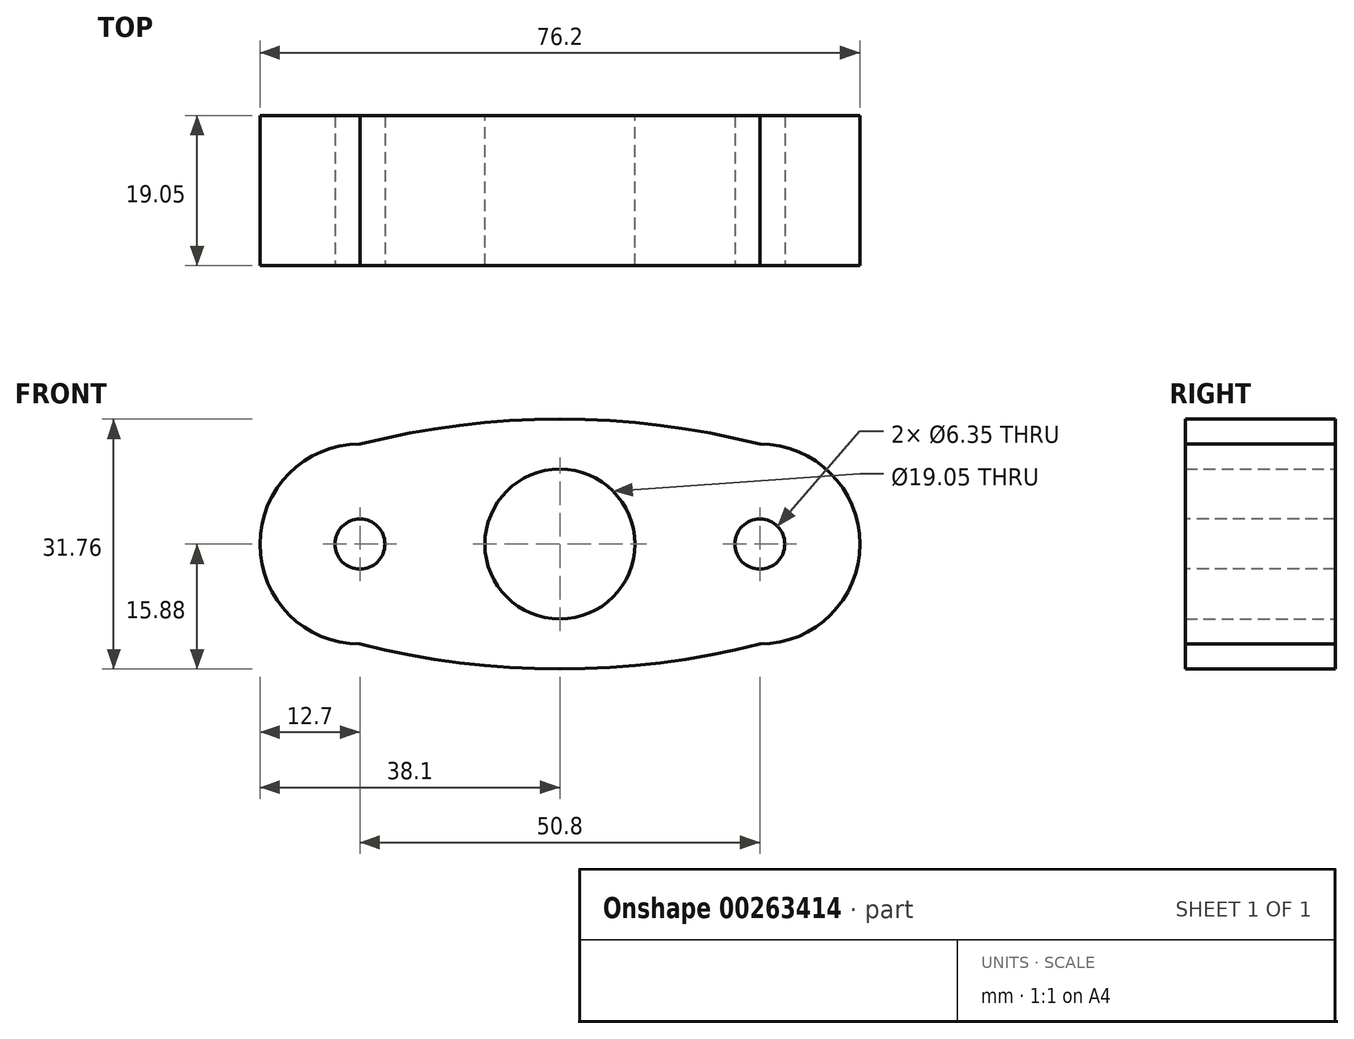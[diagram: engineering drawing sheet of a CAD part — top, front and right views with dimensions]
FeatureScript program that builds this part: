
annotation { "Feature Type Name" : "Feature", "Feature Type Description" : "" }
export const myFeature = defineFeature(function(context is Context, id is Id, definition is map)
    precondition{}
    {
        {
            var Q0;
            Q0=qCreatedBy(makeId("Front.planeOp"),FACE);
            var sketch = newSketch(context, id + "F0", { "sketchPlane" : qUnion([Q0])});
            skLineSegment(sketch, "E0.bottom", {"start": v(25.4, 12.7) * mm, "end": v(-25.4, 12.7) * mm});
            skLineSegment(sketch, "E0.top", {"start": v(25.4, -12.7) * mm, "end": v(-25.4, -12.7) * mm});
            skLineSegment(sketch, "E0.left", {"start": v(25.4, 12.7) * mm, "end": v(25.4, -12.7) * mm});
            skLineSegment(sketch, "E0.right", {"start": v(-25.4, 12.7) * mm, "end": v(-25.4, -12.7) * mm});
            skPoint(sketch, "E0.middle", {"position": v(0, 0) * mm});
            skArc(sketch, "E1", {"start": v(-25.4, 12.7) * mm, "mid": v(-38.1, 0) * mm, "end": v(-25.4, -12.7) * mm});
            skArc(sketch, "E2", {"start": v(25.4, -12.7) * mm, "mid": v(38.1, 0) * mm, "end": v(25.4, 12.7) * mm});
            skArc(sketch, "E3", {"start": v(25.4, 12.7) * mm, "mid": v(0, 15.87) * mm, "end": v(-25.4, 12.7) * mm});
            skArc(sketch, "E4", {"start": v(-25.4, -12.7) * mm, "mid": v(0, -15.88) * mm, "end": v(25.4, -12.7) * mm});
            skSolve(sketch);
        }
        {
            var Q0;
            Q0 = qSketchRegion(id + "F0", true);
            extrude(context, id + "F1", {"entities" : qUnion([Q0]), "depth" : 19.05 * mm});
        }
        {
            var Q0;
            Q0=sQuery(id+"F0.wireOp",VERTEX,"E0.middle");
            var Q1;
            Q1=makeQuery(id+"F1.opExtrude","SWEPT_BODY",BODY,{"disambiguationData":[OSD([sQuery(id+"F0.wireOp",EDGE,"E1"),sQuery(id+"F0.wireOp",EDGE,"E2"),sQuery(id+"F0.wireOp",EDGE,"E3"),sQuery(id+"F0.wireOp",EDGE,"E4")])]});
            hole(context, id + "F2", {"style" : HoleStyle.SIMPLE, "endStyle" : HoleEndStyle.THROUGH, "oppositeDirection" : true, "holeDiameter" : 19.05 * mm, "tappedDepth" : 12.7 * mm, "tapClearance" : 3, "locations" : qUnion([Q0]), "scope" : qUnion([Q1])});
        }
        {
            var Q0;
            Q0=makeQuery(id+"F1.opExtrude","CAP_FACE",FACE,{"disambiguationData":[OSD([sQuery(id+"F0.wireOp",EDGE,"E1"),sQuery(id+"F0.wireOp",EDGE,"E2"),sQuery(id+"F0.wireOp",EDGE,"E3"),sQuery(id+"F0.wireOp",EDGE,"E4")])],"isStart":false});
            var sketch = newSketch(context, id + "F3", { "sketchPlane" : qUnion([Q0])});
            skPoint(sketch, "E5", {"position": v(-25.4, 0) * mm});
            skPoint(sketch, "E6", {"position": v(25.4, 0) * mm});
            skSolve(sketch);
        }
        {
            var Q0;
            Q0=sQuery(id+"F3.wireOp",VERTEX,"E5");
            var Q1;
            Q1=sQuery(id+"F3.wireOp",VERTEX,"E6");
            var Q2;
            Q2=makeQuery(id+"F1.opExtrude","SWEPT_BODY",BODY,{"disambiguationData":[OSD([sQuery(id+"F0.wireOp",EDGE,"E1"),sQuery(id+"F0.wireOp",EDGE,"E2"),sQuery(id+"F0.wireOp",EDGE,"E3"),sQuery(id+"F0.wireOp",EDGE,"E4")])]});
            hole(context, id + "F4", {"style" : HoleStyle.SIMPLE, "endStyle" : HoleEndStyle.THROUGH, "holeDiameter" : 6.35 * mm, "tappedDepth" : 12.7 * mm, "tapClearance" : 3, "locations" : qUnion([Q0, Q1]), "scope" : qUnion([Q2])});
        }
    });
